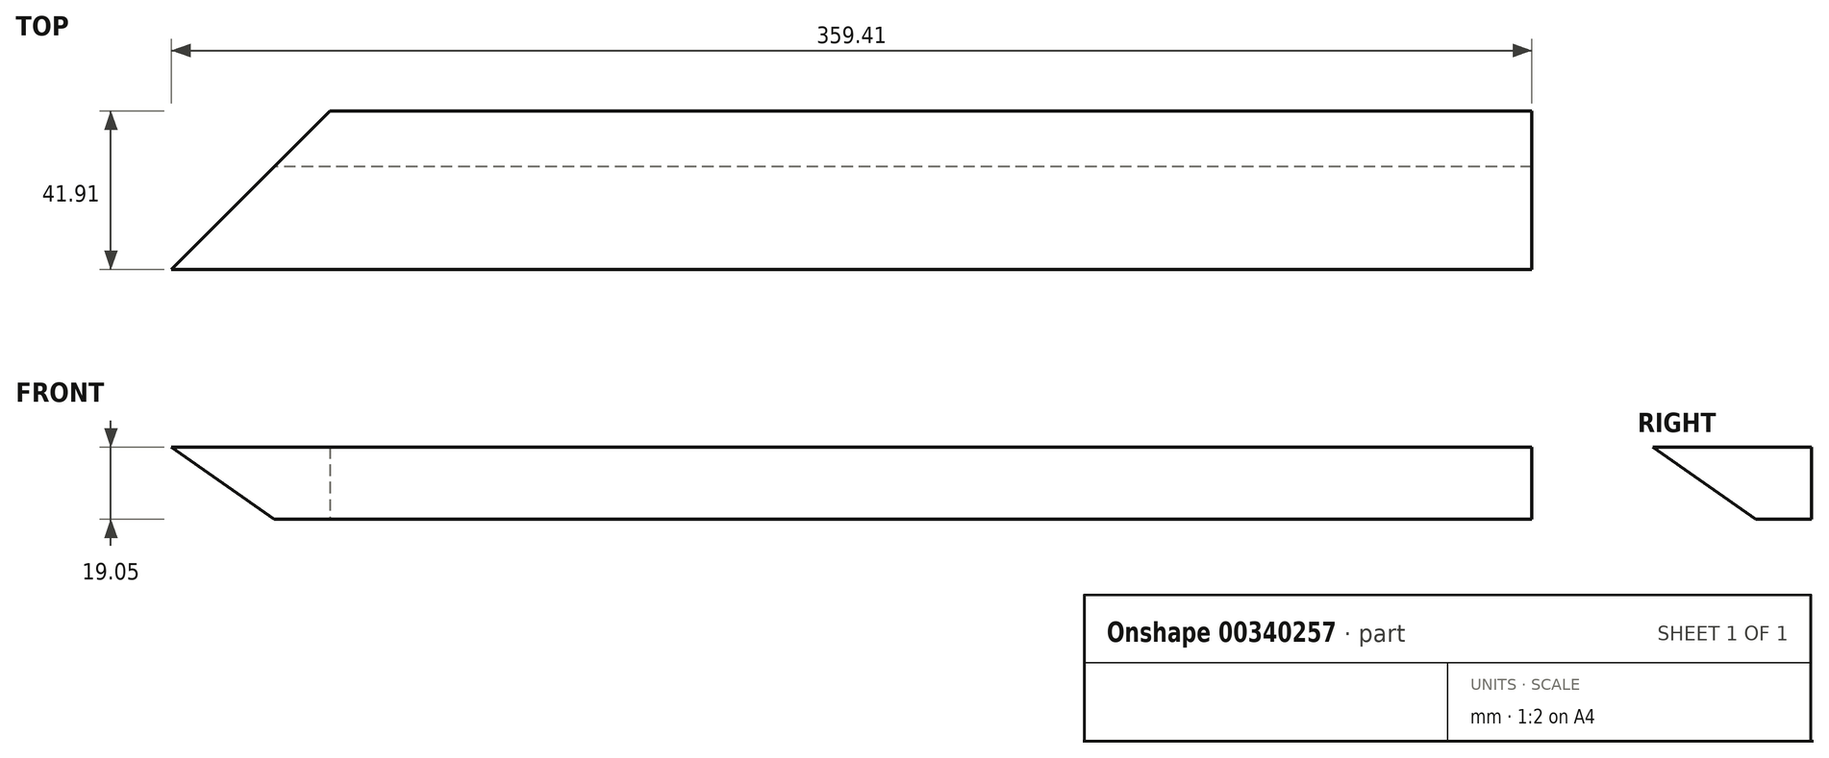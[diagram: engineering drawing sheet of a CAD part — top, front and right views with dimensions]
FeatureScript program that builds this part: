
annotation { "Feature Type Name" : "Feature", "Feature Type Description" : "" }
export const myFeature = defineFeature(function(context is Context, id is Id, definition is map)
    precondition{}
    {
        {
            var Q0;
            Q0=qCreatedBy(makeId("Right.planeOp"),FACE);
            var sketch = newSketch(context, id + "F0", { "sketchPlane" : qUnion([Q0])});
            skLineSegment(sketch, "E0.bottom", {"start": v(0, 19.05) * mm, "end": v(-41.91, 19.05) * mm});
            skLineSegment(sketch, "E0.top", {"start": v(0, 0) * mm, "end": v(-14.7, 0) * mm});
            skLineSegment(sketch, "E0.left", {"start": v(0, 19.05) * mm, "end": v(0, 0) * mm});
            skPoint(sketch, "E0.middle", {"position": v(0, 0) * mm});
            skLineSegment(sketch, "E1", {"start": v(-41.91, 19.05) * mm, "end": v(-14.7, 0) * mm});
            skSolve(sketch);
        }
        {
            var Q0;
            Q0=qSketchRegion(id+"F0",true);
            var Q1;
            Q1 = qSketchRegion(id + "F2", true);
            extrude(context, id + "F1", {"entities" : qUnion([Q0, Q1]), "depth" : 228.6 * mm, "hasSecondDirection" : true, "secondDirectionOppositeDirection" : true, "secondDirectionDepth" : 228.6 * mm});
        }
        {
            var Q0;
            Q0=qCreatedBy(makeId("Top.planeOp"),FACE);
            var sketch = newSketch(context, id + "F2", { "sketchPlane" : qUnion([Q0])});
            skLineSegment(sketch, "E2", {"start": v(-88.9, 0) * mm, "end": v(88.9, 0) * mm, "construction": true});
            skLineSegment(sketch, "E3", {"start": v(0, 0) * mm, "end": v(0, -29.83) * mm, "construction": true});
            skLineSegment(sketch, "E4", {"start": v(-88.9, 0) * mm, "end": v(-237.74, 0) * mm});
            skLineSegment(sketch, "E5", {"start": v(-237.74, 0) * mm, "end": v(-237.74, -148.84) * mm});
            skLineSegment(sketch, "E6", {"start": v(-237.74, -148.84) * mm, "end": v(-88.9, 0) * mm});
            skSolve(sketch);
        }
        {
            var Q0;
            Q0=qSketchRegion(id+"F2",true);
            extrude(context, id + "F3", {"entities" : qUnion([Q0]), "operationType" : NewBodyOperationType.REMOVE, "endBound" : BoundingType.THROUGH_ALL, "depth" : 25.4 * mm});
        }
    });
